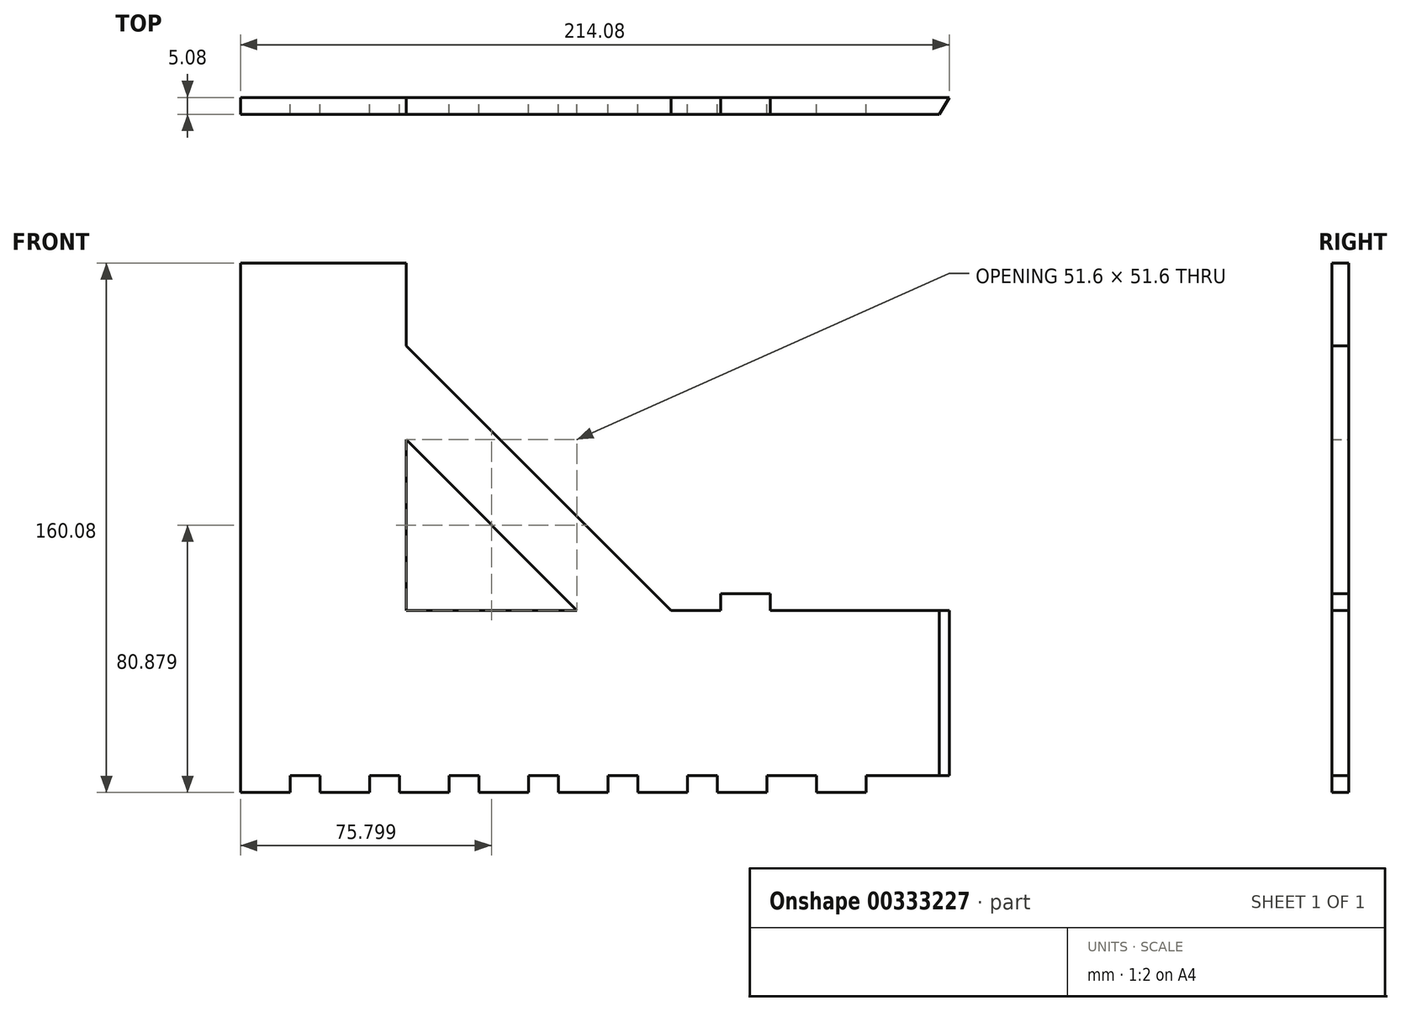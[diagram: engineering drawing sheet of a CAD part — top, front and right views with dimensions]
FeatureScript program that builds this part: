
annotation { "Feature Type Name" : "Feature", "Feature Type Description" : "" }
export const myFeature = defineFeature(function(context is Context, id is Id, definition is map)
    precondition{}
    {
        {
            var Q0;
            Q0=qCreatedBy(makeId("Front.planeOp"),FACE);
            var sketch = newSketch(context, id + "F0", { "sketchPlane" : qUnion([Q0])});
            skLineSegment(sketch, "E0", {"start": v(-32.42, 0) * mm, "end": v(-246.5, 0) * mm});
            skLineSegment(sketch, "E1", {"start": v(-246.5, 0) * mm, "end": v(-246.5, 130) * mm});
            skLineSegment(sketch, "E2", {"start": v(-246.5, 130) * mm, "end": v(-196.5, 130) * mm});
            skLineSegment(sketch, "E3", {"start": v(-196.5, 130) * mm, "end": v(-196.5, 50) * mm});
            skLineSegment(sketch, "E4", {"start": v(-196.5, 50) * mm, "end": v(-32.42, 50) * mm});
            skLineSegment(sketch, "E5", {"start": v(-196.5, 130) * mm, "end": v(-116.5, 50) * mm});
            skLineSegment(sketch, "E6", {"start": v(-196.5, 101.6) * mm, "end": v(-144.9, 50) * mm});
            skLineSegment(sketch, "E7", {"start": v(-246.5, 0) * mm, "end": v(-246.5, -5.08) * mm});
            skLineSegment(sketch, "E8", {"start": v(-246.5, -5.08) * mm, "end": v(-231.5, -5.08) * mm});
            skLineSegment(sketch, "E9", {"start": v(-231.5, -5.08) * mm, "end": v(-231.5, 0) * mm});
            skLineSegment(sketch, "E10.1.0.0", {"start": v(-207.5, -5.08) * mm, "end": v(-207.5, 0) * mm});
            skLineSegment(sketch, "E10.1.0.1", {"start": v(-222.5, -5.08) * mm, "end": v(-207.5, -5.08) * mm});
            skLineSegment(sketch, "E10.1.0.2", {"start": v(-222.5, 0) * mm, "end": v(-222.5, -5.08) * mm});
            skLineSegment(sketch, "E10.2.0.0", {"start": v(-183.5, -5.08) * mm, "end": v(-183.5, 0) * mm});
            skLineSegment(sketch, "E10.2.0.1", {"start": v(-198.5, -5.08) * mm, "end": v(-183.5, -5.08) * mm});
            skLineSegment(sketch, "E10.2.0.2", {"start": v(-198.5, 0) * mm, "end": v(-198.5, -5.08) * mm});
            skLineSegment(sketch, "E10.3.0.0", {"start": v(-159.5, -5.08) * mm, "end": v(-159.5, 0) * mm});
            skLineSegment(sketch, "E10.3.0.1", {"start": v(-174.5, -5.08) * mm, "end": v(-159.5, -5.08) * mm});
            skLineSegment(sketch, "E10.3.0.2", {"start": v(-174.5, 0) * mm, "end": v(-174.5, -5.08) * mm});
            skLineSegment(sketch, "E10.4.0.0", {"start": v(-135.5, -5.08) * mm, "end": v(-135.5, 0) * mm});
            skLineSegment(sketch, "E10.4.0.1", {"start": v(-150.5, -5.08) * mm, "end": v(-135.5, -5.08) * mm});
            skLineSegment(sketch, "E10.4.0.2", {"start": v(-150.5, 0) * mm, "end": v(-150.5, -5.08) * mm});
            skLineSegment(sketch, "E10.5.0.0", {"start": v(-111.5, -5.08) * mm, "end": v(-111.5, 0) * mm});
            skLineSegment(sketch, "E10.5.0.1", {"start": v(-126.5, -5.08) * mm, "end": v(-111.5, -5.08) * mm});
            skLineSegment(sketch, "E10.5.0.2", {"start": v(-126.5, 0) * mm, "end": v(-126.5, -5.08) * mm});
            skLineSegment(sketch, "E10.6.0.0", {"start": v(-87.5, -5.08) * mm, "end": v(-87.5, 0) * mm});
            skLineSegment(sketch, "E10.6.0.1", {"start": v(-102.5, -5.08) * mm, "end": v(-87.5, -5.08) * mm});
            skLineSegment(sketch, "E10.6.0.2", {"start": v(-102.5, 0) * mm, "end": v(-102.5, -5.08) * mm});
            skLineSegment(sketch, "E10.direction1", {"start": v(-246.5, -5.08) * mm, "end": v(-222.5, -5.08) * mm, "construction": true});
            skLineSegment(sketch, "E11", {"start": v(-32.42, 50) * mm, "end": v(-32.42, 0) * mm});
            skPoint(sketch, "E12.start.orphan", {"position": v(0, 50) * mm});
            skSolve(sketch);
        }
        {
            var Q0;
            Q0=qSketchRegion(id+"F0",true);
            extrude(context, id + "F1", {"entities" : qUnion([Q0]), "depth" : 5.08 * mm});
        }
        {
            var Q0;
            Q0=makeQuery(id+"F1.opExtrude","SWEPT_FACE",FACE,{"disambiguationData":[OSD([sQuery(id+"F0.wireOp",EDGE,"E2")])]});
            var Q1;
            Q1=makeQuery(id+"F1.opExtrude","SWEPT_FACE",FACE,{"disambiguationData":[OSD([sQuery(id+"F0.wireOp",EDGE,"0f3f7d79-0024-4810-854d-b7a6c9fa19c64.MirrorCS")])]});
            extrude(context, id + "F2", {"entities" : qUnion([Q0, Q1]), "operationType" : NewBodyOperationType.ADD, "depth" : 25 * mm});
        }
        {
            var Q0;
            {var subQ0=sQuery(id+"F0.wireOp",EDGE,"E0");Q0=makeQuery(id+"F1.opExtrude","SWEPT_FACE",FACE,{"disambiguationData":[OSD([subQ0]),TDD([makeQuery(id+"F0.imprint","IMPRINT",EDGE,{"disambiguationData":[TD([[makeQuery(id+"F0.imprint","INTERSECT",VERTEX,{"derivedFrom":[subQ0,sQuery(id+"F0.wireOp",EDGE,"E11")]}),-1.0]])],"derivedFrom":subQ0})])]});}
            var sketch = newSketch(context, id + "F3", { "sketchPlane" : qUnion([Q0])});
            skLineSegment(sketch, "E13", {"start": v(-35.35, 0) * mm, "end": v(-35.35, 5.08) * mm});
            skLineSegment(sketch, "E14", {"start": v(-35.35, 5.08) * mm, "end": v(-32.42, 0) * mm});
            skSolve(sketch);
        }
        {
            var Q0;
            {var subQ0=sQuery(id+"F3.wireOp",EDGE,"E14");Q0=makeQuery(id+"F3.imprint","IMPRINT",FACE,{"disambiguationData":[TD([[makeQuery(id+"F3.imprint","IMPRINT",EDGE,{"derivedFrom":subQ0}),1.0]])]});}
            extrude(context, id + "F4", {"entities" : qUnion([Q0]), "operationType" : NewBodyOperationType.REMOVE, "oppositeDirection" : true, "depth" : 55.7 * mm});
        }
        {
            var Q0;
            {var subQ0=sQuery(id+"F0.wireOp",EDGE,"E0");Q0=makeQuery(id+"F1.opExtrude","SWEPT_FACE",FACE,{"disambiguationData":[OSD([subQ0]),TDD([makeQuery(id+"F0.imprint","IMPRINT",EDGE,{"disambiguationData":[TD([[makeQuery(id+"F0.imprint","INTERSECT",VERTEX,{"derivedFrom":[subQ0,sQuery(id+"F0.wireOp",EDGE,"E11")]}),-1.0]])],"derivedFrom":subQ0})])]});}
            var sketch = newSketch(context, id + "F5", { "sketchPlane" : qUnion([Q0])});
            skLineSegment(sketch, "E15.bottom", {"start": v(-72.5, 5.08) * mm, "end": v(-57.5, 5.08) * mm});
            skLineSegment(sketch, "E15.top", {"start": v(-72.5, 0) * mm, "end": v(-57.5, 0) * mm});
            skLineSegment(sketch, "E15.right", {"start": v(-57.5, 5.08) * mm, "end": v(-57.5, 0) * mm});
            skLineSegment(sketch, "E16", {"start": v(-72.5, 5.08) * mm, "end": v(-72.5, 0) * mm});
            skPoint(sketch, "E15.left.start.orphan", {"position": v(-87.5, 5.08) * mm});
            skPoint(sketch, "E17.orphan", {"position": v(-87.5, 0) * mm});
            skSolve(sketch);
        }
        {
            var Q0;
            Q0=qSketchRegion(id+"F5",true);
            extrude(context, id + "F6", {"entities" : qUnion([Q0]), "operationType" : NewBodyOperationType.ADD, "depth" : 5.08 * mm});
        }
        {
            var Q0;
            {var subQ0=sQuery(id+"F0.wireOp",EDGE,"E4");Q0=makeQuery(id+"F1.opExtrude","SWEPT_FACE",FACE,{"disambiguationData":[OSD([subQ0]),TDD([makeQuery(id+"F0.imprint","IMPRINT",EDGE,{"disambiguationData":[TD([[makeQuery(id+"F0.imprint","INTERSECT",VERTEX,{"derivedFrom":[subQ0,sQuery(id+"F0.wireOp",EDGE,"E11")]}),1.0]])],"derivedFrom":subQ0})])]});}
            var sketch = newSketch(context, id + "F7", { "sketchPlane" : qUnion([Q0])});
            skLineSegment(sketch, "E18.bottom", {"start": v(-101.5, 0) * mm, "end": v(-86.5, 0) * mm});
            skLineSegment(sketch, "E18.top", {"start": v(-101.5, -5.08) * mm, "end": v(-86.5, -5.08) * mm});
            skLineSegment(sketch, "E18.right", {"start": v(-86.5, 0) * mm, "end": v(-86.5, -5.08) * mm});
            skLineSegment(sketch, "E19", {"start": v(-101.5, 0) * mm, "end": v(-101.5, -5.08) * mm});
            skPoint(sketch, "E18.left.end.orphan", {"position": v(-116.5, -5.08) * mm});
            skPoint(sketch, "E18.left.start.orphan", {"position": v(-116.5, 0) * mm});
            skSolve(sketch);
        }
        {
            var Q0;
            Q0=qSketchRegion(id+"F7",true);
            extrude(context, id + "F8", {"entities" : qUnion([Q0]), "operationType" : NewBodyOperationType.ADD, "depth" : 5.08 * mm});
        }
    });
